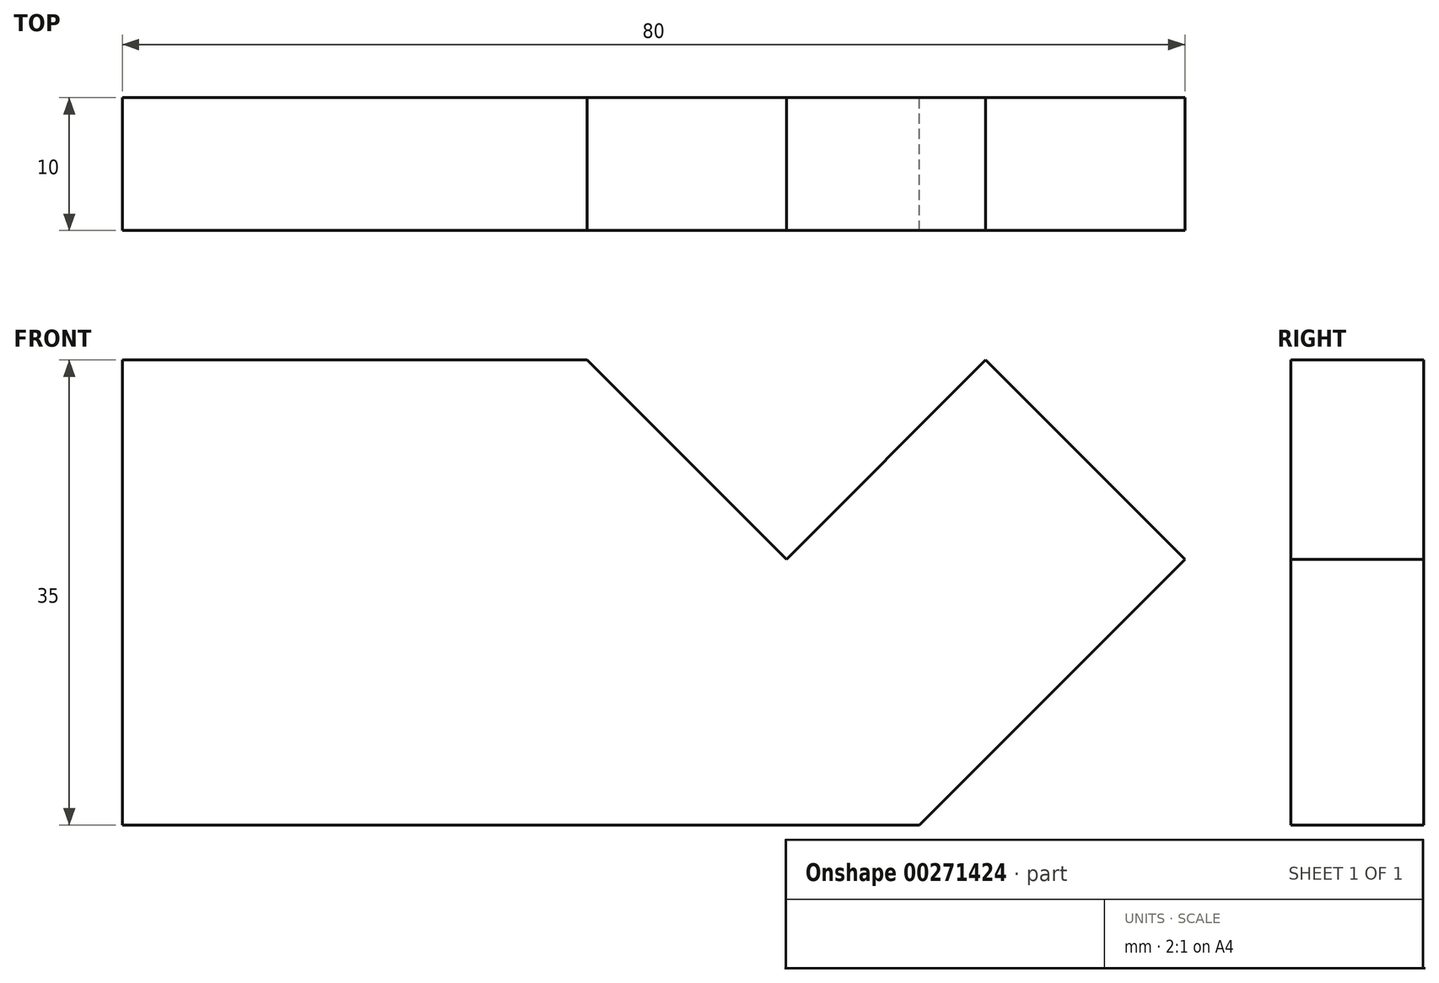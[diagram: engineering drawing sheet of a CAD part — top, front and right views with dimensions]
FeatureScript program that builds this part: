
annotation { "Feature Type Name" : "Feature", "Feature Type Description" : "" }
export const myFeature = defineFeature(function(context is Context, id is Id, definition is map)
    precondition{}
    {
        {
            var Q0;
            Q0=qCreatedBy(makeId("Front.planeOp"),FACE);
            var sketch = newSketch(context, id + "F0", { "sketchPlane" : qUnion([Q0])});
            skLineSegment(sketch, "E0", {"start": v(0, 35) * mm, "end": v(0, 0) * mm});
            skLineSegment(sketch, "E1", {"start": v(0, 0) * mm, "end": v(60, 0) * mm});
            skLineSegment(sketch, "E2", {"start": v(60, 0) * mm, "end": v(80, 20) * mm});
            skLineSegment(sketch, "E3", {"start": v(0, 35) * mm, "end": v(35, 35) * mm});
            skLineSegment(sketch, "E4", {"start": v(35, 35) * mm, "end": v(50, 20) * mm});
            skLineSegment(sketch, "E5", {"start": v(50, 20) * mm, "end": v(65, 35) * mm});
            skLineSegment(sketch, "E6", {"start": v(65, 35) * mm, "end": v(80, 20) * mm});
            skSolve(sketch);
        }
        {
            var Q0;
            Q0 = qSketchRegion(id + "F0", true);
            extrude(context, id + "F1", {"entities" : qUnion([Q0]), "depth" : 10 * mm});
        }
    });
